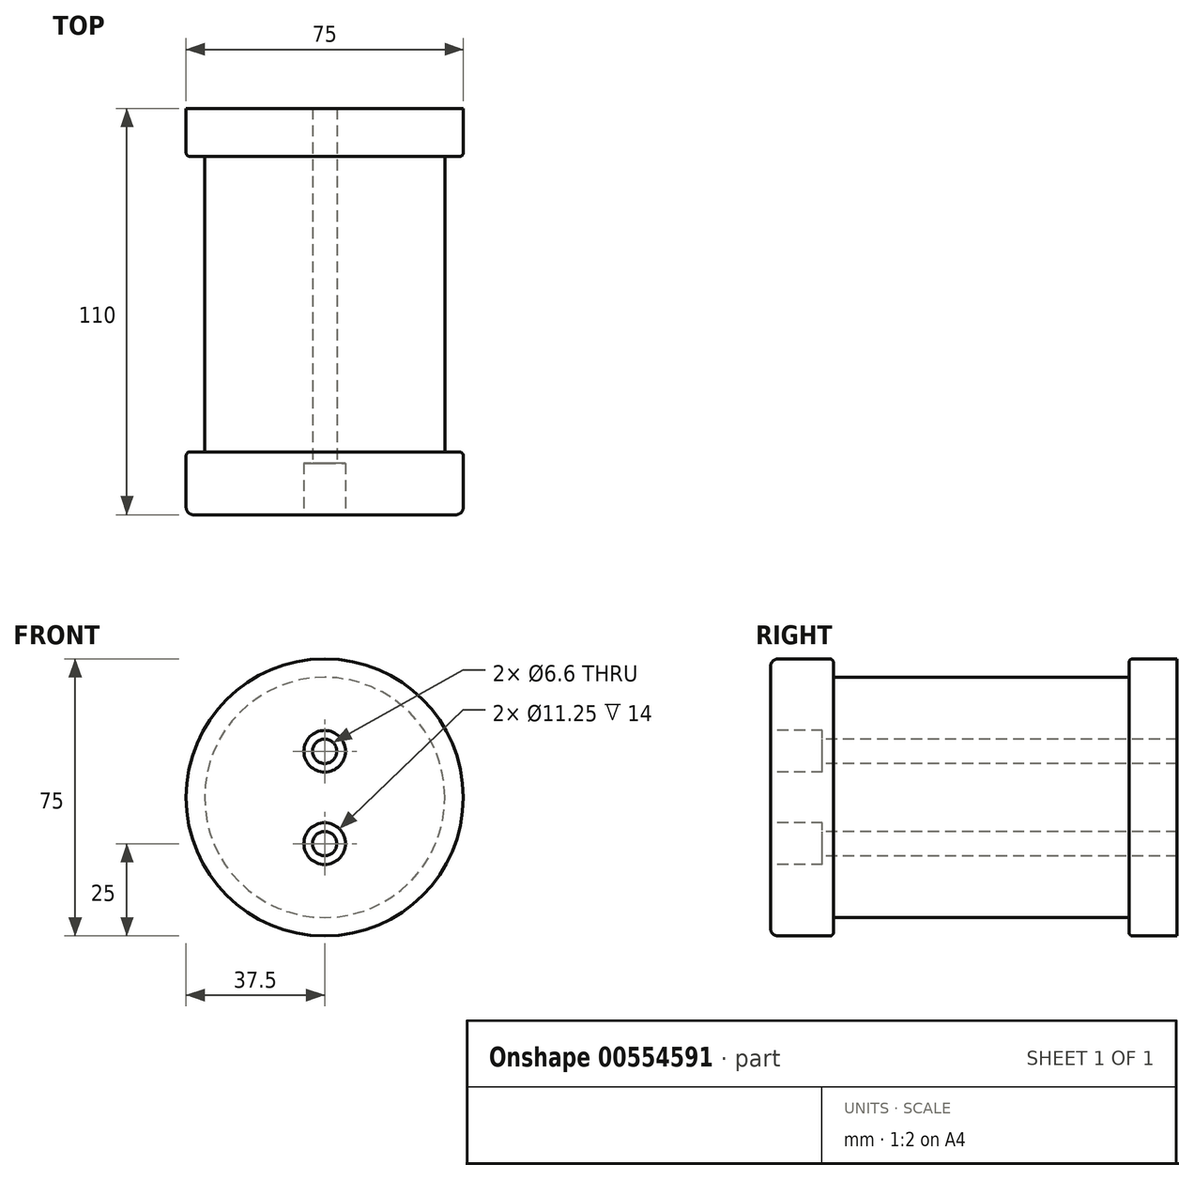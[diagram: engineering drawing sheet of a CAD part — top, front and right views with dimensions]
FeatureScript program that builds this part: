
annotation { "Feature Type Name" : "Feature", "Feature Type Description" : "" }
export const myFeature = defineFeature(function(context is Context, id is Id, definition is map)
    precondition{}
    {
        {
            var Q0;
            Q0=qCreatedBy(makeId("Front.planeOp"),FACE);
            var sketch = newSketch(context, id + "F0", { "sketchPlane" : qUnion([Q0])});
            skCircle(sketch, "E0", {"center": v(0, 0) * mm, "radius": 32.5 * mm});
            skSolve(sketch);
        }
        {
            var Q0;
            Q0=makeQuery(id+"F0.imprint","IMPRINT",FACE,{"disambiguationData":[TD([[makeQuery(id+"F0.imprint","IMPRINT",EDGE,{"derivedFrom":sQuery(id+"F0.wireOp",EDGE,"E0")}),1.0]])]});
            extrude(context, id + "F1", {"entities" : qUnion([Q0]), "depth" : 80 * mm, "offsetDistance" : 25 * mm});
        }
        {
            var Q0;
            Q0=qCreatedBy(makeId("Front.planeOp"),FACE);
            var sketch = newSketch(context, id + "F2", { "sketchPlane" : qUnion([Q0])});
            skCircle(sketch, "E1", {"center": v(0, 0) * mm, "radius": 37.5 * mm});
            skSolve(sketch);
        }
        {
            var Q0;
            Q0=makeQuery(id+"F2.imprint","IMPRINT",FACE,{"disambiguationData":[TD([[makeQuery(id+"F2.imprint","IMPRINT",EDGE,{"derivedFrom":sQuery(id+"F2.wireOp",EDGE,"E1")}),1.0]])]});
            extrude(context, id + "F3", {"entities" : qUnion([Q0]), "operationType" : NewBodyOperationType.ADD, "oppositeDirection" : true, "depth" : 13 * mm, "offsetDistance" : 25 * mm});
        }
        {
            var Q0;
            Q0=makeQuery(id+"F1.opExtrude","CAP_FACE",FACE,{"disambiguationData":[OSD([sQuery(id+"F0.wireOp",EDGE,"E0")])],"isStart":false});
            var sketch = newSketch(context, id + "F4", { "sketchPlane" : qUnion([Q0])});
            skCircle(sketch, "E2", {"center": v(0, 0) * mm, "radius": 37.5 * mm});
            skSolve(sketch);
        }
        {
            var Q0;
            Q0 = qSketchRegion(id + "F4", true);
            extrude(context, id + "F5", {"entities" : qUnion([Q0]), "operationType" : NewBodyOperationType.ADD, "depth" : 17 * mm, "offsetDistance" : 25 * mm});
        }
        {
            var Q0;
            Q0=makeQuery(id+"F1.opExtrude","CAP_EDGE",EDGE,{"disambiguationData":[OSD([sQuery(id+"F0.wireOp",EDGE,"E0")])],"isStart":true});
            var Q1;
            Q1=makeQuery(id+"F5.opExtrude","CAP_EDGE",EDGE,{"disambiguationData":[OSD([sQuery(id+"F4.wireOp",EDGE,"E2")])],"isStart":false});
            var Q2;
            Q2=makeQuery(id+"F1.opExtrude","CAP_EDGE",EDGE,{"disambiguationData":[OSD([sQuery(id+"F0.wireOp",EDGE,"E0")])],"isStart":false});
            fillet(context, id + "F6", {"entities" : qUnion([Q0, Q1, Q2]), "radius" : 2 * mm, "tangentPropagation" : true, "allowEdgeOverflow" : false});
        }
        {
            var Q0;
            Q0=makeQuery(id+"F5.opExtrude","CAP_FACE",FACE,{"disambiguationData":[OSD([sQuery(id+"F4.wireOp",EDGE,"E2")])],"isStart":false});
            var sketch = newSketch(context, id + "F7", { "sketchPlane" : qUnion([Q0])});
            skPoint(sketch, "E3", {"position": v(0, 12.5) * mm});
            skPoint(sketch, "E4", {"position": v(0, -12.5) * mm});
            skSolve(sketch);
        }
        {
            var Q0;
            Q0=sQuery(id+"F7.wireOp",VERTEX,"E3");
            var Q1;
            Q1=sQuery(id+"F7.wireOp",VERTEX,"E4");
            var Q2;
            Q2=makeQuery(id+"F1.opExtrude","SWEPT_BODY",BODY,{"disambiguationData":[OSD([sQuery(id+"F0.wireOp",EDGE,"E0")])]});
            hole(context, id + "F8", {"style" : HoleStyle.C_BORE, "endStyle" : HoleEndStyle.THROUGH, "holeDiameter" : 6.6 * mm, "cBoreDiameter" : 11.25 * mm, "cBoreDepth" : 14 * mm, "isTappedThrough" : true, "tappedDepth" : 8 * mm, "tapClearance" : 3, "startFromSketch" : true, "locations" : qUnion([Q0, Q1]), "scope" : qUnion([Q2])});
        }
        {
            var Q0;
            Q0=makeQuery(id+"F3.opExtrude","CAP_EDGE",EDGE,{"disambiguationData":[OSD([sQuery(id+"F2.wireOp",EDGE,"E1")])],"isStart":true});
            var Q1;
            Q1=makeQuery(id+"F5.opExtrude","CAP_EDGE",EDGE,{"disambiguationData":[OSD([sQuery(id+"F4.wireOp",EDGE,"E2")])],"isStart":true});
            fillet(context, id + "F9", {"entities" : qUnion([Q0, Q1]), "radius" : 1 * mm, "tangentPropagation" : true, "allowEdgeOverflow" : false});
        }
    });
